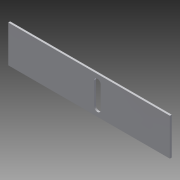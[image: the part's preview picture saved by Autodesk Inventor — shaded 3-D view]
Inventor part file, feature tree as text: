
AUTODESK INVENTOR PART (.ipt)
format: ipt  version: 2013 (Build 170138000, 138)  size: 83,968 bytes
history: native  units: in
note: dims shown in document units (in); Inventor stores cm internally (conversion verified against a paired STEP export)
features: extrude x2, sketch x2
ambient origin geometry x8: Origin, YZ Plane, XZ Plane, XY Plane, X Axis, Y Axis, Z Axis, Center Point
bodies: Solid1 (feature_tree)
feature tree (4):
  extrude  "Extrusion1"  Depth=5.0in
  extrude  "Extrusion2"  Depth=3.0in
  sketch  "Sketch1"  dims[d0=21.75in d1=5.0in]
  sketch  "Sketch2"  dims[d2=0.25in d3=0.0in d4=3.0in d6=0.44in d7=9.75in d8=1.0in d9=0.25in d10=0.0in]
